# Revit family: FU_Modular_Sandler_Bau 5-5
name_source: partatom
category: Furniture
units: mm (PartAtom-declared; Revit-internal decimal feet)

## family parameters
Always vertical = Yes
Cut with Voids When Loaded = No
OmniClass Number = 23.21.23.00
Render Appearance Source = Family Geometry
Room Calculation Point = No
Shared = No
Work Plane-Based = No

## types (1)
- Bau 5.5
    Default Elevation = 0 mm  [stored 0 ft]
    Depth = 950 mm  [stored 3.1168 ft]
    Description = Large corner element with concave curve. Part of the unconventional, award-winning Bau modular seating.
    Height = 720 mm  [stored 2.3622 ft]
    Manufacturer = Sandler
    Model = Bau 5.5
    Product Material = Fabric - Manhattan - Staten YI386
    URL = https://www.sandlerseating.com
    Version = 1
    Weight Net (Kg) = 31
    Width = 1600 mm  [stored 5.24934 ft]

note: [stored X ft] marks values corroborated as IEEE doubles in the binary element streams (Revit-internal decimal feet)

## geometry (parser evidence)
native form markers: Sweep x2
no freeform markers — native parametric forms only
